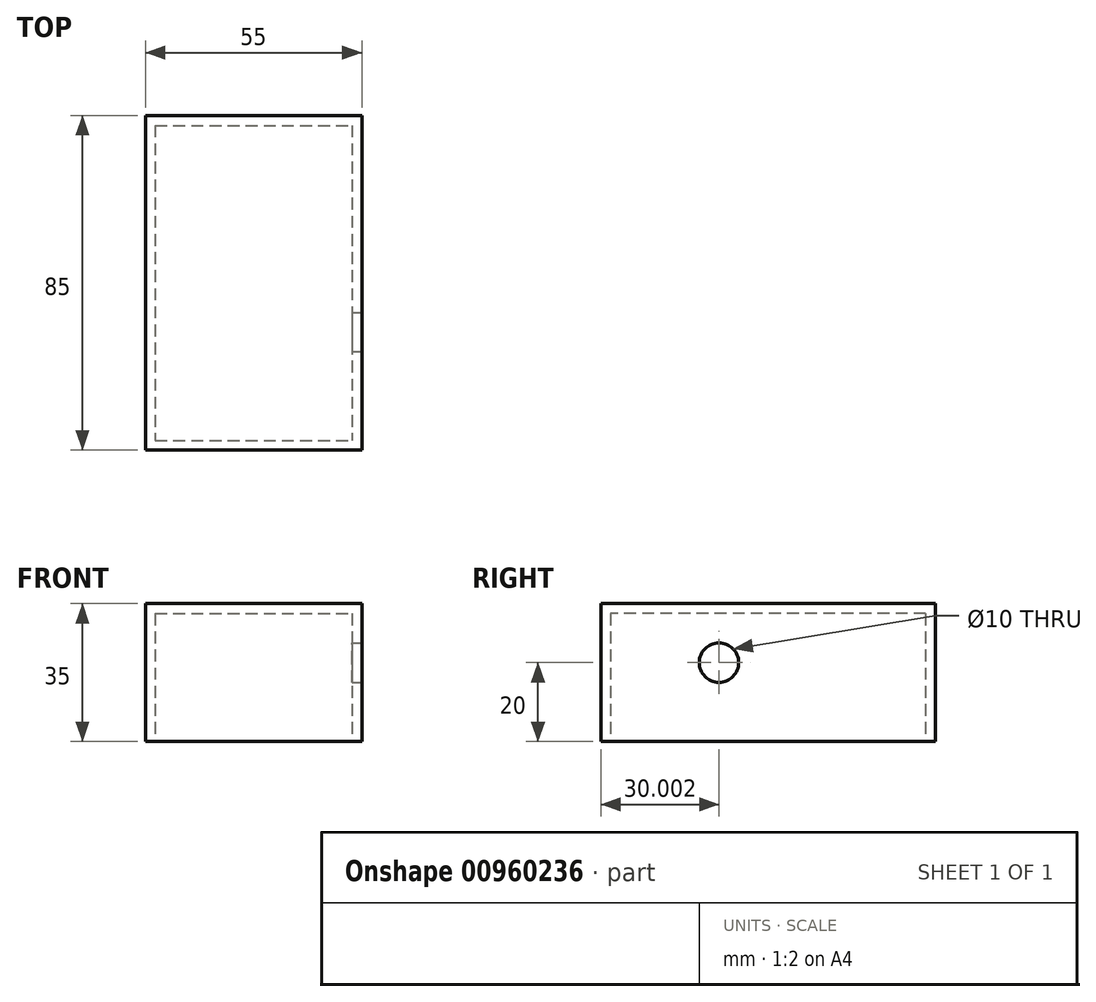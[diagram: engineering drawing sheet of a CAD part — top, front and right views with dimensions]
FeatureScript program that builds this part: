
annotation { "Feature Type Name" : "Feature", "Feature Type Description" : "" }
export const myFeature = defineFeature(function(context is Context, id is Id, definition is map)
    precondition{}
    {
        {
            var Q0;
            Q0=qCreatedBy(makeId("Top.planeOp"),FACE);
            var sketch = newSketch(context, id + "F0", { "sketchPlane" : qUnion([Q0])});
            skLineSegment(sketch, "E0.bottom", {"start": v(-55.61, 53.61) * mm, "end": v(-0.61, 53.61) * mm});
            skLineSegment(sketch, "E0.top", {"start": v(-55.61, -31.39) * mm, "end": v(-0.61, -31.39) * mm});
            skLineSegment(sketch, "E0.left", {"start": v(-55.61, 53.61) * mm, "end": v(-55.61, -31.39) * mm});
            skLineSegment(sketch, "E0.right", {"start": v(-0.61, 53.61) * mm, "end": v(-0.61, -31.39) * mm});
            skSolve(sketch);
        }
        {
            var Q0;
            Q0 = qSketchRegion(id + "F0", true);
            extrude(context, id + "F1", {"entities" : qUnion([Q0]), "depth" : 35 * mm, "offsetDistance" : 25.4 * mm});
        }
        {
            var Q0;
            Q0=makeQuery(id+"F1.opExtrude","SWEPT_FACE",FACE,{"disambiguationData":[OSD([sQuery(id+"F0.wireOp",EDGE,"E0.right")])]});
            var sketch = newSketch(context, id + "F2", { "sketchPlane" : qUnion([Q0])});
            skSolve(sketch);
        }
        {
            var Q0;
            Q0=makeQuery(id+"F1.opExtrude","CAP_FACE",FACE,{"disambiguationData":[OSD([sQuery(id+"F0.wireOp",EDGE,"E0.bottom"),sQuery(id+"F0.wireOp",EDGE,"E0.top"),sQuery(id+"F0.wireOp",EDGE,"E0.left"),sQuery(id+"F0.wireOp",EDGE,"E0.right")])],"isStart":true});
            shell(context, id + "F3", {"entities" : qUnion([Q0]), "thickness" : 2.5 * mm});
        }
        {
            var Q0;
            {var subQ0=sQuery(id+"F0.wireOp",EDGE,"E0.right");Q0=makeQuery(id+"F2.imprint","IMPRINT",FACE,{"disambiguationData":[TD([[makeQuery(id+"F2.imprint","IMPRINT",EDGE,{"derivedFrom":makeQuery(id+"F1.opExtrude","CAP_EDGE",EDGE,{"disambiguationData":[OSD([subQ0])],"isStart":true})}),-1.0]])]});}
            var sketch = newSketch(context, id + "F4", { "sketchPlane" : qUnion([Q0])});
            skCircle(sketch, "E1", {"center": v(-1.39, 20) * mm, "radius": 5 * mm});
            skSolve(sketch);
        }
        {
            var Q0;
            Q0=makeQuery(id+"F4.imprint","IMPRINT",FACE,{"disambiguationData":[TD([[makeQuery(id+"F4.imprint","IMPRINT",EDGE,{"derivedFrom":sQuery(id+"F4.wireOp",EDGE,"E1")}),1.0]])]});
            extrude(context, id + "F5", {"entities" : qUnion([Q0]), "operationType" : NewBodyOperationType.REMOVE, "oppositeDirection" : true, "depth" : 25 * mm, "offsetDistance" : 25 * mm});
        }
        {
            var Q0;
            Q0=makeQuery(id+"F1.opExtrude","CAP_FACE",FACE,{"disambiguationData":[OSD([sQuery(id+"F0.wireOp",EDGE,"E0.bottom"),sQuery(id+"F0.wireOp",EDGE,"E0.top"),sQuery(id+"F0.wireOp",EDGE,"E0.left"),sQuery(id+"F0.wireOp",EDGE,"E0.right")])],"isStart":false});
            var sketch = newSketch(context, id + "F6", { "sketchPlane" : qUnion([Q0])});
            skLineSegment(sketch, "E2", {"start": v(-28.11, 22.19) * mm, "end": v(-28.11, 47.19) * mm});
            skArc(sketch, "E3.0.startCap", {"start": v(-24.11, 22.19) * mm, "mid": v(-28.11, 18.19) * mm, "end": v(-32.11, 22.19) * mm});
            skArc(sketch, "E3.0.endCap", {"start": v(-32.11, 47.19) * mm, "mid": v(-28.11, 51.19) * mm, "end": v(-24.11, 47.19) * mm});
            skLineSegment(sketch, "E3.0.left", {"start": v(-32.11, 22.19) * mm, "end": v(-32.11, 47.19) * mm});
            skLineSegment(sketch, "E3.0.right", {"start": v(-24.11, 22.19) * mm, "end": v(-24.11, 47.19) * mm});
            skSolve(sketch);
        }
        {
            var Q0;
            Q0=makeQuery(id+"F6.imprint","IMPRINT",FACE,{"disambiguationData":[TD([[makeQuery(id+"F6.imprint","IMPRINT",EDGE,{"derivedFrom":sQuery(id+"F6.wireOp",EDGE,"E3.0.startCap")}),1.0]])]});
            var sketch = newSketch(context, id + "F7", { "sketchPlane" : qUnion([Q0])});
            skSolve(sketch);
        }
        {
            var Q0;
            Q0=sQuery(id+"F6.wireOp",EDGE,"E3.0.endCap");
            var Q1;
            Q1=sQuery(id+"F6.wireOp",EDGE,"E3.0.left");
            var Q2;
            Q2=sQuery(id+"F6.wireOp",EDGE,"E3.0.right");
            var Q3;
            Q3=sQuery(id+"F6.wireOp",EDGE,"E3.0.startCap");
            extrude(context, id + "F8", {"bodyType" : ToolBodyType.SURFACE, "surfaceEntities" : qUnion([Q0, Q1, Q2, Q3]), "depth" : 25 * mm, "offsetDistance" : 25 * mm});
        }
    });
